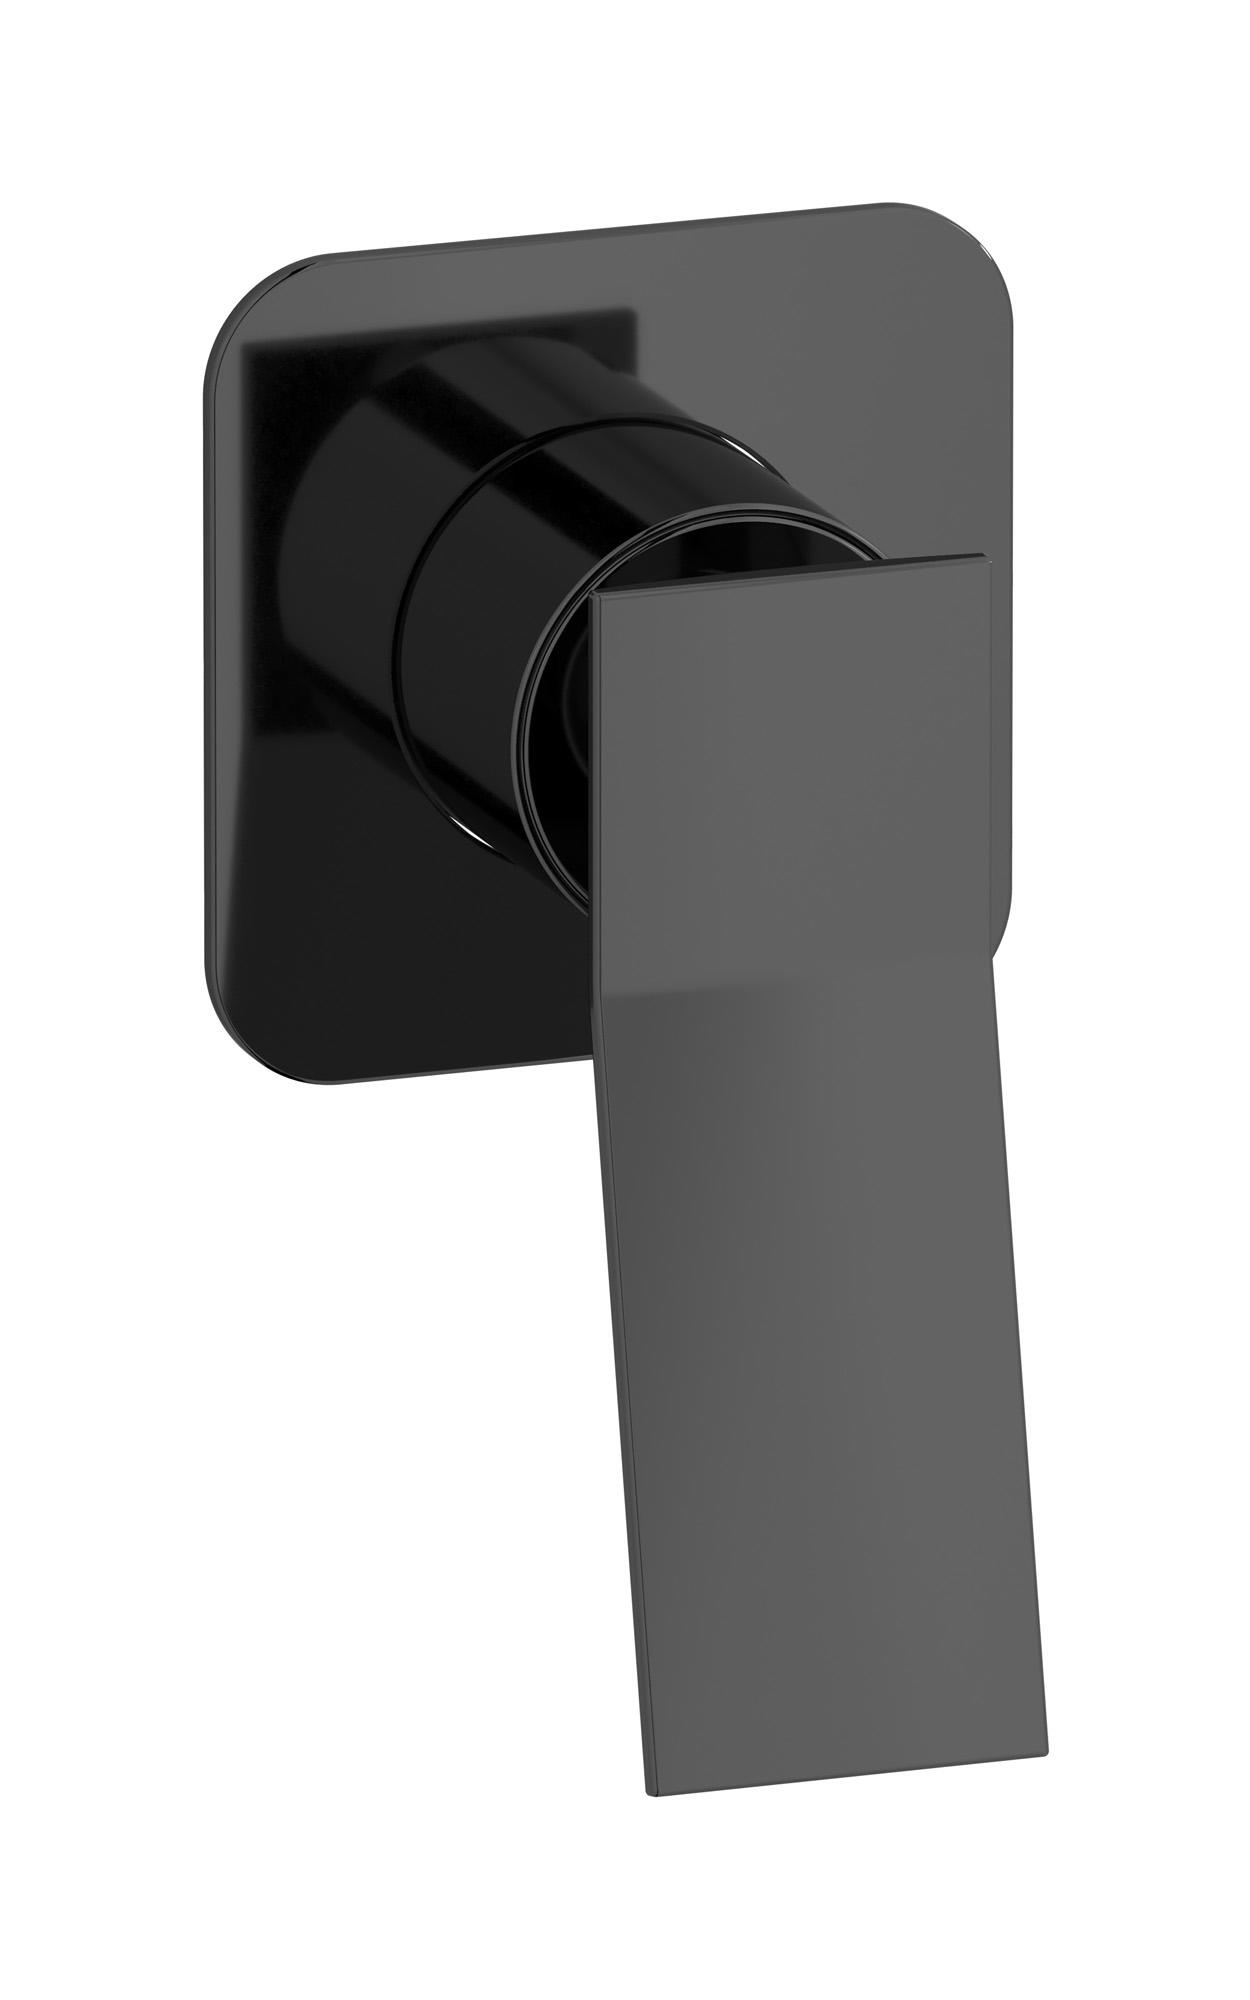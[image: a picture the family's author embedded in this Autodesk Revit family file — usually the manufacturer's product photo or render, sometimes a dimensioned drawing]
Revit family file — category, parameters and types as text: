
# Revit family: WA300
name_source: partatom
category: Apparecchi idraulici
units: mm (PartAtom-declared; Revit-internal decimal feet)

## family parameters
Basato su piano di lavoro = No
Condiviso = No
Mantieni orientamento annotazione = No
Numero OmniClass = 23.45.55.17
Punto di calcolo locali = No
Quota connettore circolare = Usa diametro
Sempre verticale = Sì
Taglio con vuoti quando caricato = No
Tipo di parte = Normale
Titolo OmniClass = Mixing Faucets

## types (12) — shared parameters
Cold water inlet = 10 mm  [stored 0.0328084 ft]
Commenti sul tipo = Wall mixer
Connessione CW = No
Connessione HW = No
Connessione di scarico = No
Connessione di ventilazione = No
Descrizione = Exposed parts for manual wall mixer
Hot water inlet = 10 mm  [stored 0.0328084 ft]
Produttore = IB Rubinetterie S.p.A.
URL = https://www.weareib.it
zero-valued in all types: Prospetto di default

## per-type parameters (varying)
| type | Finishes surface | Immagine tipo | Modello |
| Chrome | IB_Chrome | WA300CC.jpg | WA300CC |
| Brushed nickel | IB_Brushed nickel | WA300SS.jpg | WA300SS |
| Matt black | IB_matt black | WA300NP.jpg | WA300NP |
| Matt white | IB_matt white | WA300BO.jpg | WA300BO |
| Black chrome | IB_Black chrome | WA300CF.jpg | WA300CF |
| Brushed black chrome | IB_Brushed black chrome | WA300CS.jpg | WA300CS |
| Pale gold | IB_Pale gold | WA300II.jpg | WA300II |
| Brushed pale gold | IB_brushed pale gold | WA300IS.jpg | WA300IS |
| Rose gold | IB_Rose gold | WA300RS.jpg | WA300RS |
| Brushed rose gold | IB_Brushed rose gold | WA300SR.jpg | WA300SR |
| Gold | IB_gold | WA300OO.jpg | WA300OO |
| Brushed gold | IB_brushed gold | WA300OS.jpg | WA300OS |

note: [stored X ft] marks values corroborated as IEEE doubles in the binary element streams (Revit-internal decimal feet)
